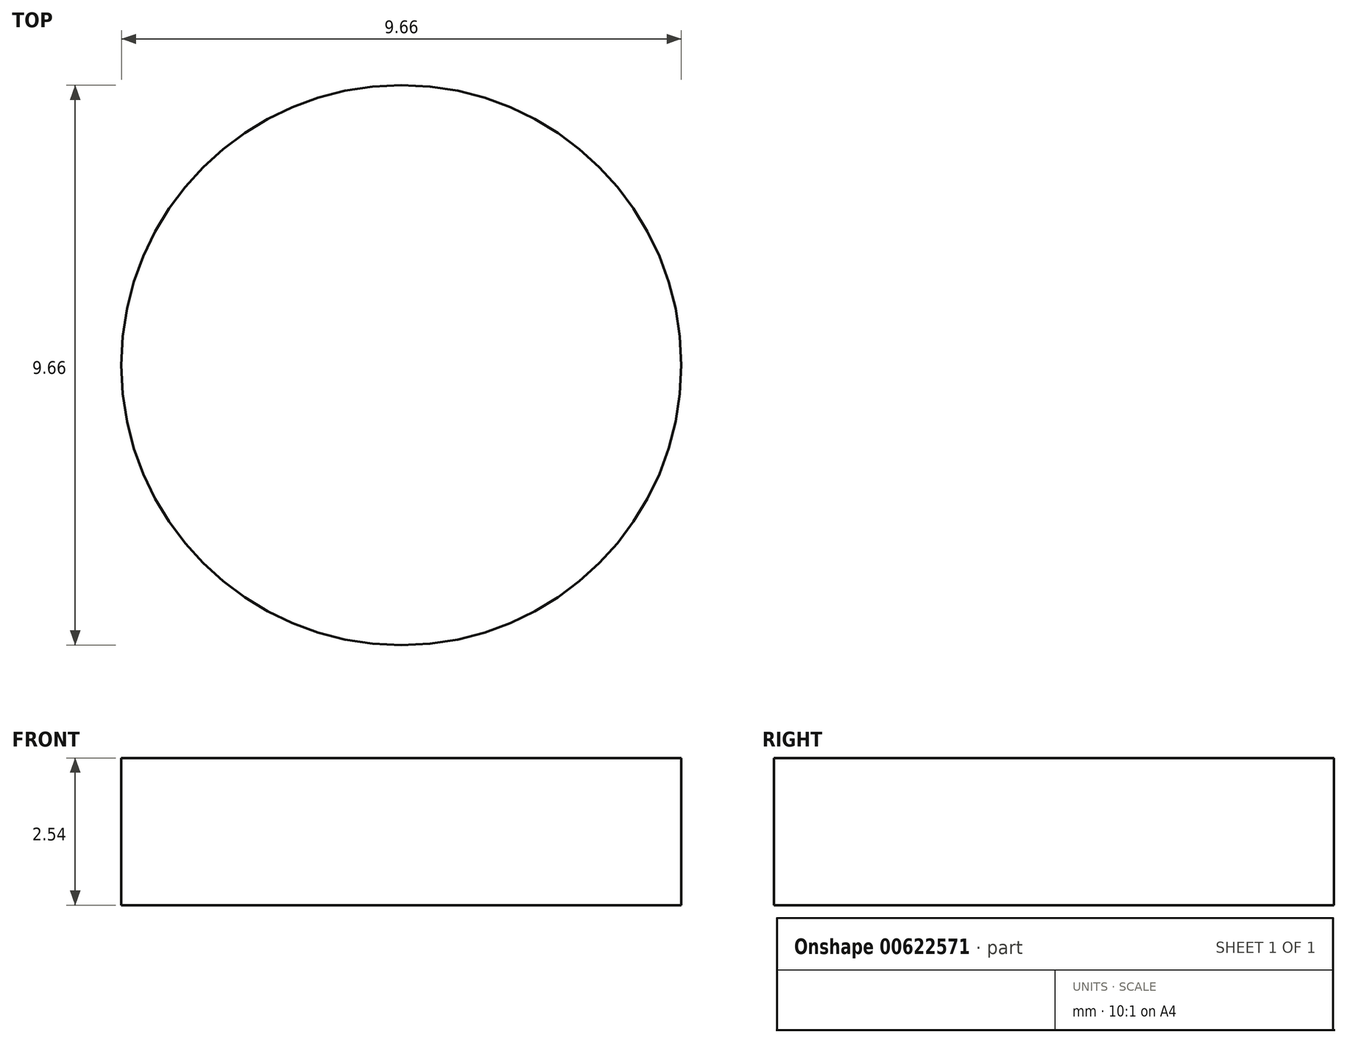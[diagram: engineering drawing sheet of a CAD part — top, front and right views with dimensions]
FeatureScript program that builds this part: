
annotation { "Feature Type Name" : "Feature", "Feature Type Description" : "" }
export const myFeature = defineFeature(function(context is Context, id is Id, definition is map)
    precondition{}
    {
        {
            var Q0;
            Q0=qCreatedBy(makeId("Top.planeOp"),FACE);
            var sketch = newSketch(context, id + "F0", { "sketchPlane" : qUnion([Q0])});
            skCircle(sketch, "E0", {"center": v(-132.07, 0) * mm, "radius": 4.83 * mm});
            skCircle(sketch, "E1.0.1.0", {"center": v(-132.07, 25.4) * mm, "radius": 4.83 * mm});
            skCircle(sketch, "E1.1.0.0", {"center": v(-106.67, 0) * mm, "radius": 4.83 * mm});
            skCircle(sketch, "E1.1.1.0", {"center": v(-106.67, 25.4) * mm, "radius": 4.83 * mm});
            skCircle(sketch, "E1.2.0.0", {"center": v(-81.27, 0) * mm, "radius": 4.83 * mm});
            skCircle(sketch, "E1.2.1.0", {"center": v(-81.27, 25.4) * mm, "radius": 4.83 * mm});
            skCircle(sketch, "E1.3.0.0", {"center": v(-55.87, 0) * mm, "radius": 4.83 * mm});
            skCircle(sketch, "E1.3.1.0", {"center": v(-55.87, 25.4) * mm, "radius": 4.83 * mm});
            skCircle(sketch, "E1.4.0.0", {"center": v(-30.47, 0) * mm, "radius": 4.83 * mm});
            skCircle(sketch, "E1.4.1.0", {"center": v(-30.47, 25.4) * mm, "radius": 4.83 * mm});
            skLineSegment(sketch, "E1.direction1", {"start": v(-132.07, 0) * mm, "end": v(-106.67, 0) * mm, "construction": true});
            skLineSegment(sketch, "E1.direction2", {"start": v(-132.07, 0) * mm, "end": v(-132.07, 25.4) * mm, "construction": true});
            skSolve(sketch);
        }
        {
            var Q0;
            Q0=sQuery(id+"F0.wireOp",EDGE,"E0");
            extrude(context, id + "F1", {"bodyType" : ToolBodyType.SURFACE, "surfaceEntities" : qUnion([Q0]), "endBound" : BoundingType.SYMMETRIC, "depth" : 2.54 * mm, "hasOffset" : true, "offsetDistance" : 2.54 * mm});
        }
    });
